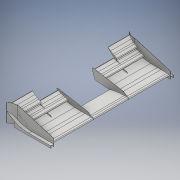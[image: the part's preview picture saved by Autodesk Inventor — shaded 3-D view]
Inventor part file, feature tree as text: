
AUTODESK INVENTOR PART (.ipt)
format: ipt  version: 2018 (Build 220112000, 112)  size: 919,552 bytes
history: native  units: mm
features: extrude x16, sketch x16, projected_geometry x12, other x4, chamfer x1, mirror x1
ambient origin geometry x8: Origin, YZ Plane, XZ Plane, XY Plane, X Axis, Y Axis, Z Axis, Center Point
bodies: Body1 (feature_tree)
feature tree (50):
  extrude  "押し出し7"  Depth=394.0mm TaperAngle=0.0deg
  extrude  "押し出し8"  Depth=5.0mm TaperAngle=0.0deg
  extrude  "押し出し9"  Depth=225.0mm TaperAngle=0.0deg
  extrude  "押し出し10"  Depth=5.0mm TaperAngle=0.0deg
  extrude  "押し出し11"  Depth=225.0mm TaperAngle=0.0deg
  extrude  "押し出し13"  Depth=2.0mm
  other  "厚み1"
  other  "厚み2"
  chamfer  "面取り1"  Distance=5.0mm
  extrude  "押し出し16"  Depth=225.0mm TaperAngle=0.0deg
  extrude  "押し出し17"  Depth=1.0mm
  extrude  "押し出し18"  Depth=1.0mm
  extrude  "押し出し20"  Depth=2.0mm
  extrude  "押し出し21"  Depth=2.0mm TaperAngle=45.0deg
  extrude  "押し出し22"  Depth=10.0mm TaperAngle=0.0deg
  extrude  "押し出し23"  Depth=5.0mm
  other  "面を削除1"
  extrude  "押し出し24"  Depth=2.0mm
  extrude  "押し出し25"  TaperAngle=0.0deg  [1 undecoded]
  extrude  "押し出し27"  Depth=35.0mm TaperAngle=0.0deg
  mirror  "ミラー5"
  other  "ソリッド36"
  sketch  "スケッチ8"
  projected_geometry  "投影ループ7"
  sketch  "スケッチ9"
  projected_geometry  "投影ループ8"
  sketch  "スケッチ10"
  projected_geometry  "投影ループ9"
  projected_geometry  "投影ループ10"
  sketch  "スケッチ11"
  projected_geometry  "投影ループ11"
  sketch  "スケッチ12"
  projected_geometry  "投影ループ12"
  projected_geometry  "投影ループ13"
  projected_geometry  "投影ループ14"
  sketch  "スケッチ14"
  projected_geometry  "投影ループ16"
  sketch  "スケッチ18"
  sketch  "スケッチ19"
  sketch  "スケッチ20"
  sketch  "スケッチ21"
  sketch  "スケッチ22"
  sketch  "スケッチ23"
  projected_geometry  "投影ループ18"
  sketch  "スケッチ24"
  projected_geometry  "投影ループ19"
  sketch  "スケッチ25"
  projected_geometry  "投影ループ20"
  sketch  "スケッチ26"
  sketch  "スケッチ27"
note: 1 required parameter value undecoded (feature->parameter linkage not recoverable at this tier; creation-order binding heuristic only, values carry confidence <= 0.55)
